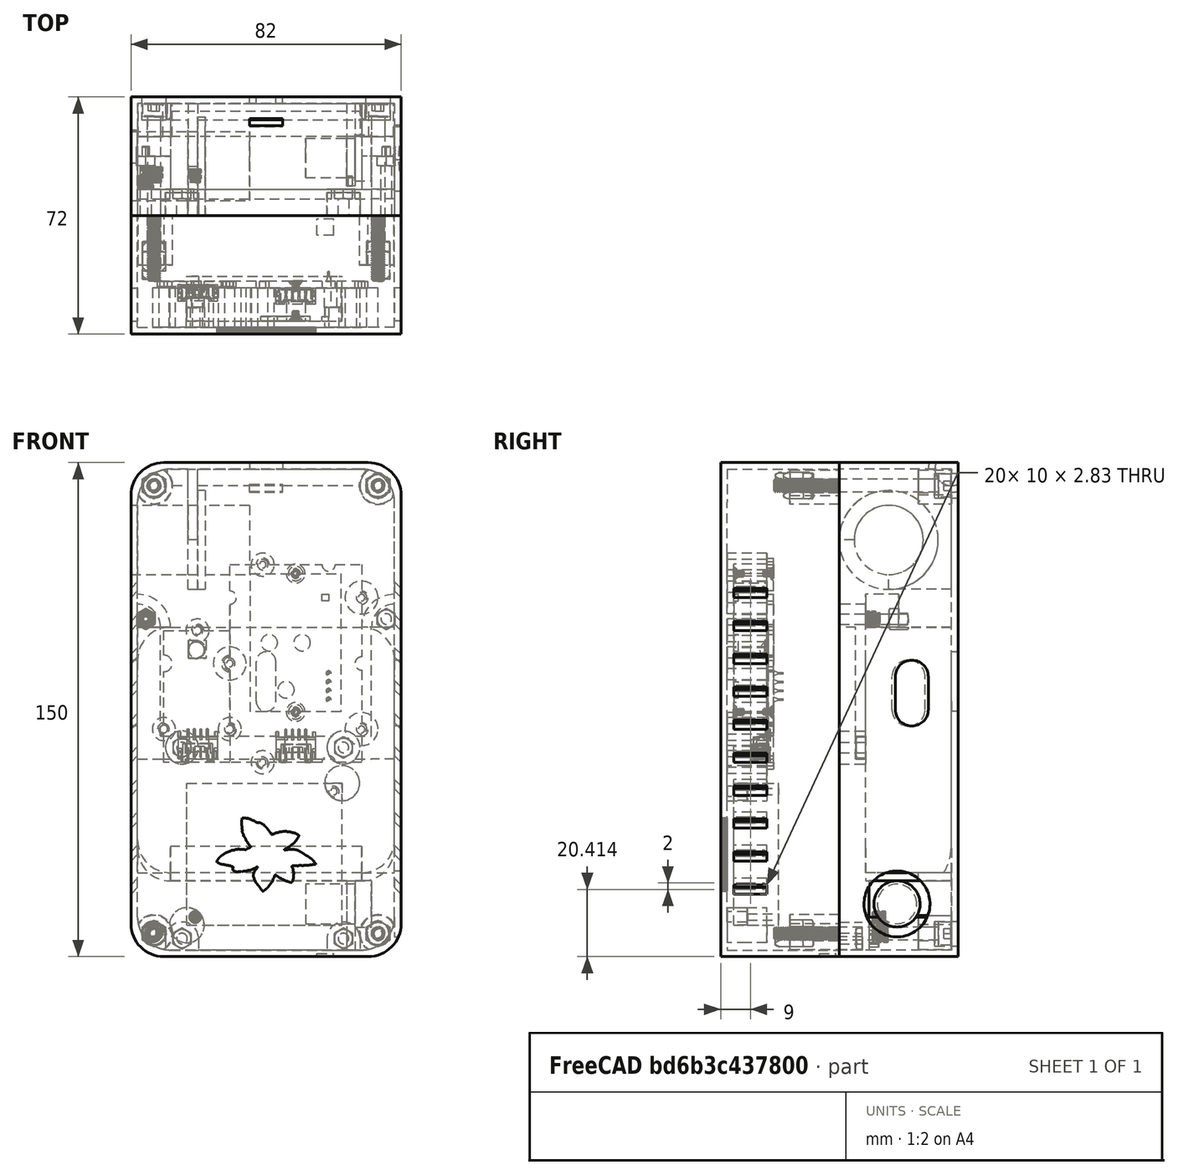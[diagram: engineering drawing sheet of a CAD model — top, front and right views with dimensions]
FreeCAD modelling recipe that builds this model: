
FCSTD DOCUMENT  (FreeCAD 0.20R29410 (Git))
Label: wearableRenewed_10_13_2022
License: All rights reserved
LicenseURL: http://en.wikipedia.org/wiki/All_rights_reserved
objects: Part::Cylinder×120, Part::MultiFuse×80, Part::Cut×73, Part::Box×72, Part::Feature×57, Part::FeaturePython×2
note: 404 computed .brp shape members not serialized (recipe doc carries the construction recipe); baked Part::Feature solids carry a one-line shape summary decoded from their .brp

FEATURE [Part::Feature] Feature  label="Odroid-C4"
  Placement = pos=(66,-10,0) rot=(0.57735,-0.57735,0.57735;2.0944rad)
  shape: bbox 57.1 x 20.65 x 89.5 mm, 2775 faces, 0 solids (baked)
FEATURE [Part::Feature] Feature001  label="SCD30"
  Placement = pos=(-1.3e-14,-22,57) rot=(0,-1,0;1.5708rad)
  shape: bbox 44 x 15.1 x 64 mm, 422 faces, 13 solids (baked)
FEATURE [Part::Feature] Feature002  label="bme280"
  Placement = pos=(-60,-20,58) rot=(0.707107,0,0.707107;3.14159rad)
  shape: bbox 23.8 x 6.016 x 41.9 mm, 221 faces, 2 solids (baked)
FEATURE [Part::MultiFuse] Fusion  label="i2cSensors"
  Placement = pos=(68,-10,0) rot=(0,0,1;0rad)
  Shapes = -> [Feature001,Feature002]
FEATURE [Part::Box] Box  label="ips7100"
  AttacherType = Attacher::AttachEngine3D
  Height = 43.1
  Length = 47.1
  Width = 13.55
FEATURE [Part::Cylinder] Cylinder
  Angle = 360
  AttacherType = Attacher::AttachEngine3D
  FirstAngle = 0
  Height = 13.55
  Placement = pos=(2.5,13.55,2.5) rot=(1,0,0;1.5708rad)
  Radius = 1
  SecondAngle = 0
FEATURE [Part::Cylinder] Cylinder001  label="semiCut"
  Angle = 90
  AttacherType = Attacher::AttachEngine3D
  FirstAngle = 0
  Height = 4.13
  Placement = pos=(0,4.13,-9e-16) rot=(1,0,0;1.5708rad)
  Radius = 5.25
  SecondAngle = 0
FEATURE [Part::MultiFuse] Fusion001  label="ipsCut"
  Shapes = -> [Cylinder,Cylinder001]
FEATURE [Part::Cylinder] Cylinder002
  Angle = 360
  AttacherType = Attacher::AttachEngine3D
  FirstAngle = 0
  Height = 13.55
  Placement = pos=(2.5,13.55,2.5) rot=(1,0,0;1.5708rad)
  Radius = 1
  SecondAngle = 0
FEATURE [Part::Cylinder] Cylinder003  label="semiCut001"
  Angle = 90
  AttacherType = Attacher::AttachEngine3D
  FirstAngle = 0
  Height = 4.13
  Placement = pos=(0,4.13,-9e-16) rot=(1,0,0;1.5708rad)
  Radius = 5.25
  SecondAngle = 0
FEATURE [Part::MultiFuse] Fusion002  label="ipsCut001"
  Placement = pos=(47.1,0,43.1) rot=(0,1,0;3.14159rad)
  Shapes = -> [Cylinder002,Cylinder003]
FEATURE [Part::MultiFuse] Fusion003
  Shapes = -> [Fusion001,Fusion002]
FEATURE [Part::Cut] Cut  label="ips7100V"
  Base = -> Box
  Placement = pos=(15,-42,7.55) rot=(0,0,1;0rad)
  Tool = -> Fusion003
FEATURE [Part::Box] Box001  label="V25B"
  AttacherType = Attacher::AttachEngine3D
  Height = 77
  Length = 78
  Width = 26
FEATURE [Part::Cylinder] Cylinder004
  Angle = 90
  AttacherType = Attacher::AttachEngine3D
  FirstAngle = 0
  Height = 26
  Placement = pos=(0,26,-5.8e-15) rot=(1,0,0;1.5708rad)
  Radius = 10
  SecondAngle = 0
FEATURE [Part::Box] Box002  label="Cube"
  AttacherType = Attacher::AttachEngine3D
  Height = 10
  Length = 10
  Width = 26
FEATURE [Part::Cut] Cut001
  Base = -> Box002
  Placement = pos=(68,0,67) rot=(0,0,1;0rad)
  Tool = -> Cylinder004
FEATURE [Part::Box] Box003  label="Cube001"
  AttacherType = Attacher::AttachEngine3D
  Height = 10
  Length = 10
  Width = 26
FEATURE [Part::Cylinder] Cylinder005
  Angle = 90
  AttacherType = Attacher::AttachEngine3D
  FirstAngle = 0
  Height = 26
  Placement = pos=(0,26,-5.8e-15) rot=(1,0,0;1.5708rad)
  Radius = 10
  SecondAngle = 0
FEATURE [Part::Cut] Cut002
  Base = -> Box003
  Placement = pos=(68,0,10) rot=(0,1,0;1.5708rad)
  Tool = -> Cylinder005
FEATURE [Part::Box] Box004  label="Cube002"
  AttacherType = Attacher::AttachEngine3D
  Height = 10
  Length = 10
  Width = 26
FEATURE [Part::Cylinder] Cylinder006
  Angle = 90
  AttacherType = Attacher::AttachEngine3D
  FirstAngle = 0
  Height = 26
  Placement = pos=(0,26,-5.8e-15) rot=(1,0,0;1.5708rad)
  Radius = 10
  SecondAngle = 0
FEATURE [Part::Cut] Cut003
  Base = -> Box004
  Placement = pos=(10,0,10) rot=(0,1,0;3.14159rad)
  Tool = -> Cylinder006
FEATURE [Part::Box] Box005  label="Cube003"
  AttacherType = Attacher::AttachEngine3D
  Height = 10
  Length = 10
  Width = 26
FEATURE [Part::Cylinder] Cylinder007
  Angle = 90
  AttacherType = Attacher::AttachEngine3D
  FirstAngle = 0
  Height = 26
  Placement = pos=(0,26,-5.8e-15) rot=(1,0,0;1.5708rad)
  Radius = 10
  SecondAngle = 0
FEATURE [Part::Cut] Cut004
  Base = -> Box005
  Placement = pos=(10,0,67) rot=(0,-1,0;1.5708rad)
  Tool = -> Cylinder007
FEATURE [Part::MultiFuse] Fusion004  label="v25Cuts"
  Shapes = -> [Cut001,Cut002,Cut003,Cut004]
FEATURE [Part::Cut] Cut005  label="V25B001"
  Base = -> Box001
  Placement = pos=(0,-2,21) rot=(0,0,1;0rad)
  Tool = -> Fusion004
FEATURE [Part::Box] Box007  label="Cube004"
  AttacherType = Attacher::AttachEngine3D
  Height = 10
  Length = 10
  Placement = pos=(0,-10,0) rot=(0,0,1;0rad)
  Width = 36
FEATURE [Part::Cylinder] Cylinder008
  Angle = 90
  AttacherType = Attacher::AttachEngine3D
  FirstAngle = 0
  Height = 36
  Placement = pos=(0,26,-5.8e-15) rot=(1,0,0;1.5708rad)
  Radius = 10
  SecondAngle = 0
FEATURE [Part::Cut] Cut006
  Base = -> Box007
  Placement = pos=(8,18,8) rot=(0.707107,0,-0.707107;3.14159rad)
  Tool = -> Cylinder008
FEATURE [Part::Box] Box008  label="baseOut001"
  AttacherType = Attacher::AttachEngine3D
  Height = 150
  Length = 82
  Placement = pos=(80,26,-2) rot=(0,0,1;3.14159rad)
  Width = 36
FEATURE [Part::Box] Box009  label="Cube005"
  AttacherType = Attacher::AttachEngine3D
  Height = 10
  Length = 10
  Placement = pos=(0,-10,0) rot=(0,0,1;0rad)
  Width = 36
FEATURE [Part::Cylinder] Cylinder009
  Angle = 90
  AttacherType = Attacher::AttachEngine3D
  FirstAngle = 0
  Height = 36
  Placement = pos=(0,26,-5.8e-15) rot=(1,0,0;1.5708rad)
  Radius = 10
  SecondAngle = 0
FEATURE [Part::Cut] Cut007
  Base = -> Box009
  Placement = pos=(70,18,8) rot=(1,0,0;3.14159rad)
  Tool = -> Cylinder009
FEATURE [Part::Box] Box010  label="Cube006"
  AttacherType = Attacher::AttachEngine3D
  Height = 10
  Length = 10
  Placement = pos=(0,-10,0) rot=(0,0,1;0rad)
  Width = 36
FEATURE [Part::Cylinder] Cylinder010
  Angle = 90
  AttacherType = Attacher::AttachEngine3D
  FirstAngle = 0
  Height = 36
  Placement = pos=(0,26,-5.8e-15) rot=(1,0,0;1.5708rad)
  Radius = 10
  SecondAngle = 0
FEATURE [Part::Cut] Cut008
  Base = -> Box010
  Placement = pos=(8,18,138) rot=(0,0,1;3.14159rad)
  Tool = -> Cylinder010
FEATURE [Part::Box] Box011  label="Cube007"
  AttacherType = Attacher::AttachEngine3D
  Height = 10
  Length = 10
  Placement = pos=(0,-10,0) rot=(0,0,1;0rad)
  Width = 36
FEATURE [Part::Cylinder] Cylinder011
  Angle = 90
  AttacherType = Attacher::AttachEngine3D
  FirstAngle = 0
  Height = 36
  Placement = pos=(0,26,-5.8e-15) rot=(1,0,0;1.5708rad)
  Radius = 10
  SecondAngle = 0
FEATURE [Part::Cut] Cut009
  Base = -> Box011
  Placement = pos=(70,18,138) rot=(0.707107,0,0.707107;3.14159rad)
  Tool = -> Cylinder011
FEATURE [Part::MultiFuse] Fusion005
  Placement = pos=(0,-2,0) rot=(0,0,1;0rad)
  Shapes = -> [Cut006,Cut007,Cut008,Cut009]
FEATURE [Part::Cut] Cut010  label="BaseOut"
  Base = -> Box008
  Tool = -> Fusion005
FEATURE [Part::Box] Box013  label="Cube009"
  AttacherType = Attacher::AttachEngine3D
  Height = 10
  Length = 10
  Placement = pos=(0,-8,0) rot=(0,0,1;0rad)
  Width = 34
FEATURE [Part::Box] Box014  label="baseOut002"
  AttacherType = Attacher::AttachEngine3D
  Height = 146
  Length = 78
  Placement = pos=(80,26,-2) rot=(0,0,1;3.14159rad)
  Width = 34
FEATURE [Part::Box] Box015  label="Cube010"
  AttacherType = Attacher::AttachEngine3D
  Height = 10
  Length = 10
  Placement = pos=(0,-8,0) rot=(0,0,1;0rad)
  Width = 34
FEATURE [Part::Box] Box016  label="Cube011"
  AttacherType = Attacher::AttachEngine3D
  Height = 10
  Length = 10
  Placement = pos=(0,-8,0) rot=(0,0,1;0rad)
  Width = 34
FEATURE [Part::Box] Box017  label="Cube012"
  AttacherType = Attacher::AttachEngine3D
  Height = 10
  Length = 10
  Placement = pos=(0,-8,0) rot=(0,0,1;0rad)
  Width = 34
FEATURE [Part::Cylinder] Cylinder013
  Angle = 90
  AttacherType = Attacher::AttachEngine3D
  FirstAngle = 0
  Height = 34
  Placement = pos=(0,26,-5.8e-15) rot=(1,0,0;1.5708rad)
  Radius = 10
  SecondAngle = 0
FEATURE [Part::Cut] Cut012
  Base = -> Box013
  Placement = pos=(12,18,8) rot=(0.707107,0,-0.707107;3.14159rad)
  Tool = -> Cylinder013
FEATURE [Part::Cylinder] Cylinder014
  Angle = 90
  AttacherType = Attacher::AttachEngine3D
  FirstAngle = 0
  Height = 34
  Placement = pos=(0,26,-5.8e-15) rot=(1,0,0;1.5708rad)
  Radius = 10
  SecondAngle = 0
FEATURE [Part::Cut] Cut013
  Base = -> Box015
  Placement = pos=(70,18,8) rot=(1,0,0;3.14159rad)
  Tool = -> Cylinder014
FEATURE [Part::Cylinder] Cylinder015
  Angle = 90
  AttacherType = Attacher::AttachEngine3D
  FirstAngle = 0
  Height = 34
  Placement = pos=(0,26,-5.8e-15) rot=(1,0,0;1.5708rad)
  Radius = 10
  SecondAngle = 0
FEATURE [Part::Cut] Cut014
  Base = -> Box016
  Placement = pos=(12,18,134) rot=(0,0,1;3.14159rad)
  Tool = -> Cylinder015
FEATURE [Part::Cylinder] Cylinder016
  Angle = 90
  AttacherType = Attacher::AttachEngine3D
  FirstAngle = 0
  Height = 34
  Placement = pos=(0,26,-5.8e-15) rot=(1,0,0;1.5708rad)
  Radius = 10
  SecondAngle = 0
FEATURE [Part::Cut] Cut015
  Base = -> Box017
  Placement = pos=(70,18,134) rot=(0.707107,0,0.707107;3.14159rad)
  Tool = -> Cylinder016
FEATURE [Part::MultiFuse] Fusion006
  Shapes = -> [Cut012,Cut013,Cut014,Cut015]
FEATURE [Part::Cut] Cut016  label="BaseOut001"
  Base = -> Box014
  Placement = pos=(-2,-2,2) rot=(0,0,1;0rad)
  Tool = -> Fusion006
FEATURE [Part::Cut] Cut017  label="baseOut"
  Base = -> Cut010
  Tool = -> Cut016
FEATURE [Part::Box] Box018  label="Cube013"
  AttacherType = Attacher::AttachEngine3D
  Height = 10
  Length = 10
  Placement = pos=(10,26,0) rot=(0,0,1;3.14159rad)
  Width = 26
FEATURE [Part::Cylinder] Cylinder017
  Angle = 90
  AttacherType = Attacher::AttachEngine3D
  FirstAngle = 0
  Height = 26
  Placement = pos=(0,26,-5.8e-15) rot=(1,0,0;1.5708rad)
  Radius = 10
  SecondAngle = 0
FEATURE [Part::Cut] Cut018  label="batterySupport"
  Base = -> Box018
  Placement = pos=(10,-2,33.5) rot=(0,1,0;3.14159rad)
  Tool = -> Cylinder017
FEATURE [Part::Box] Box019  label="Cube014"
  AttacherType = Attacher::AttachEngine3D
  Height = 10
  Length = 10
  Placement = pos=(10,26,0) rot=(0,0,1;3.14159rad)
  Width = 26
FEATURE [Part::Cylinder] Cylinder018
  Angle = 90
  AttacherType = Attacher::AttachEngine3D
  FirstAngle = 0
  Height = 26
  Placement = pos=(0,26,-5.8e-15) rot=(1,0,0;1.5708rad)
  Radius = 10
  SecondAngle = 0
FEATURE [Part::Cut] Cut019  label="batterySupport001"
  Base = -> Box019
  Placement = pos=(68,-2,33.5) rot=(0,1,0;1.5708rad)
  Tool = -> Cylinder018
FEATURE [Part::Box] Box020  label="Cube015"
  AttacherType = Attacher::AttachEngine3D
  Height = 10
  Length = 10
  Placement = pos=(10,26,0) rot=(0,0,1;3.14159rad)
  Width = 26
FEATURE [Part::Cylinder] Cylinder019
  Angle = 90
  AttacherType = Attacher::AttachEngine3D
  FirstAngle = 0
  Height = 26
  Placement = pos=(0,26,-5.8e-15) rot=(1,0,0;1.5708rad)
  Radius = 10
  SecondAngle = 0
FEATURE [Part::Cut] Cut020  label="batterySupport002"
  Base = -> Box020
  Placement = pos=(68,-2,88) rot=(0,0,1;0rad)
  Tool = -> Cylinder019
FEATURE [Part::Box] Box021  label="Cube016"
  AttacherType = Attacher::AttachEngine3D
  Height = 10
  Length = 10
  Placement = pos=(10,26,0) rot=(0,0,1;3.14159rad)
  Width = 26
FEATURE [Part::Cylinder] Cylinder020
  Angle = 90
  AttacherType = Attacher::AttachEngine3D
  FirstAngle = 0
  Height = 26
  Placement = pos=(0,26,-5.8e-15) rot=(1,0,0;1.5708rad)
  Radius = 10
  SecondAngle = 0
FEATURE [Part::Cut] Cut021  label="batterySupport003"
  Base = -> Box021
  Placement = pos=(10,-2,88) rot=(0,-1,0;1.5708rad)
  Tool = -> Cylinder020
FEATURE [Part::Cylinder] Cylinder021
  Angle = 360
  AttacherType = Attacher::AttachEngine3D
  FirstAngle = 0
  Height = 7
  Placement = pos=(13.5,-3,3.5) rot=(1,0,0;1.5708rad)
  Radius = 5
  SecondAngle = 0
FEATURE [Part::Cylinder] Cylinder022
  Angle = 360
  AttacherType = Attacher::AttachEngine3D
  FirstAngle = 0
  Height = 8
  Placement = pos=(13.5,-2,3.5) rot=(1,0,0;1.5708rad)
  Radius = 1.6
  SecondAngle = 0
FEATURE [Part::Box] Box022  label="Cube017"
  AttacherType = Attacher::AttachEngine3D
  Height = 4
  Length = 10
  Placement = pos=(8.5,-3,4) rot=(1,0,0;3.14159rad)
  Width = 7
FEATURE [Part::Cylinder] Cylinder023
  Angle = 360
  AttacherType = Attacher::AttachEngine3D
  FirstAngle = 0
  Height = 7
  Placement = pos=(62.5,-3,3.5) rot=(1,0,0;1.5708rad)
  Radius = 5
  SecondAngle = 0
FEATURE [Part::Cylinder] Cylinder024
  Angle = 360
  AttacherType = Attacher::AttachEngine3D
  FirstAngle = 0
  Height = 8
  Placement = pos=(62.5,-2,3.5) rot=(1,0,0;1.5708rad)
  Radius = 1.6
  SecondAngle = 0
FEATURE [Part::Box] Box023  label="Cube018"
  AttacherType = Attacher::AttachEngine3D
  Height = 4
  Length = 10
  Placement = pos=(57.5,-3,4) rot=(1,0,0;3.14159rad)
  Width = 7
FEATURE [Part::Cylinder] Cylinder025
  Angle = 360
  AttacherType = Attacher::AttachEngine3D
  FirstAngle = 0
  Height = 20
  Radius = 6
  SecondAngle = 0
FEATURE [Part::Cylinder] Cylinder026
  Angle = 360
  AttacherType = Attacher::AttachEngine3D
  FirstAngle = 0
  Height = 5
  Radius = 7
  SecondAngle = 0
FEATURE [Part::MultiFuse] Fusion007  label="powerSwitch"
  Placement = pos=(71,7.5,14) rot=(0,-1,0;1.5708rad)
  Shapes = -> [Cylinder025,Cylinder026]
FEATURE [Part::Box] Box024  label="Cube019"
  AttacherType = Attacher::AttachEngine3D
  Height = 22
  Length = 2.5
  Placement = pos=(63.5,24,21) rot=(1,0,0;3.14159rad)
  Width = 25
FEATURE [Part::MultiFuse] Fusion008  label="base"
  Shapes = -> [Cut017,Cut018,Cut019,Cut020,Cut021]
FEATURE [Part::MultiFuse] Fusion009  label="base001"
  Shapes = -> [Cylinder021,Cylinder023,Box022,Box023,Box024,Fusion008]
FEATURE [Part::MultiFuse] Fusion010  label="baseCuts"
  Shapes = -> [Cylinder024,Cylinder022,Fusion007]
FEATURE [Part::Cut] Cut022  label="base002"
  Base = -> Fusion009
  Tool = -> Fusion010
FEATURE [Part::Cylinder] Cylinder027  label="mainMounts"
  Angle = 90
  AttacherType = Attacher::AttachEngine3D
  FirstAngle = 0
  Height = 10
  Placement = pos=(0,24,98) rot=(1,0,0;1.5708rad)
  Radius = 10
  SecondAngle = 0
FEATURE [Part::Cylinder] Cylinder028  label="mainMounts001"
  Angle = 90
  AttacherType = Attacher::AttachEngine3D
  FirstAngle = 0
  Height = 10
  Placement = pos=(78,24,98) rot=(0.57735,-0.57735,0.57735;2.0944rad)
  Radius = 10
  SecondAngle = 0
FEATURE [Part::Cylinder] Cylinder029
  Angle = 360
  AttacherType = Attacher::AttachEngine3D
  FirstAngle = 0
  Height = 10
  Placement = pos=(2.5,-2,100.5) rot=(1,0,0;1.5708rad)
  Radius = 1.6
  SecondAngle = 0
FEATURE [Part::Cylinder] Cylinder030
  Angle = 360
  AttacherType = Attacher::AttachEngine3D
  FirstAngle = 0
  Height = 10
  Placement = pos=(75.5,-2,100.5) rot=(1,0,0;1.5708rad)
  Radius = 1.6
  SecondAngle = 0
FEATURE [Part::MultiFuse] Fusion011  label="baseCuts001"
  Placement = pos=(0,10,0) rot=(0,0,1;0rad)
  Shapes = -> [Cylinder029,Cylinder030]
FEATURE [Part::MultiFuse] Fusion012
  Placement = pos=(0,-16,0) rot=(0,0,1;0rad)
  Shapes = -> [Cylinder028,Cylinder027]
FEATURE [Part::MultiFuse] Fusion013  label="base003"
  Shapes = -> [Cut022,Fusion012]
FEATURE [Part::Cut] Cut023  label="baseBottom"
  Base = -> Fusion013
  Tool = -> Fusion011
FEATURE [Part::Feature] Solid  label="m3HeatSet"
  Placement = pos=(2.5,2.3,100.5) rot=(1,0,0;3.14159rad)
  shape: bbox 4.772 x 4.354 x 4.772 mm, 239 faces (baked)
FEATURE [Part::Cylinder] Cylinder031
  Angle = 360
  AttacherType = Attacher::AttachEngine3D
  FirstAngle = 0
  Height = 8
  Placement = pos=(13.5,-2,61.5) rot=(1,0,0;1.5708rad)
  Radius = 5
  SecondAngle = 0
FEATURE [Part::Cylinder] Cylinder032  label="cuts"
  Angle = 360
  AttacherType = Attacher::AttachEngine3D
  FirstAngle = 0
  Height = 8
  Placement = pos=(13.5,-2,61.5) rot=(1,0,0;1.5708rad)
  Radius = 1.6
  SecondAngle = 0
FEATURE [Part::Cylinder] Cylinder034
  Angle = 360
  AttacherType = Attacher::AttachEngine3D
  FirstAngle = 0
  Height = 8
  Placement = pos=(62.5,-2,61.5) rot=(1,0,0;1.5708rad)
  Radius = 5
  SecondAngle = 0
FEATURE [Part::Cylinder] Cylinder035  label="cuts001"
  Angle = 360
  AttacherType = Attacher::AttachEngine3D
  FirstAngle = 0
  Height = 8
  Placement = pos=(62.5,-2,61.5) rot=(1,0,0;1.5708rad)
  Radius = 1.6
  SecondAngle = 0
FEATURE [Part::Cylinder] Cylinder036
  Angle = 90
  AttacherType = Attacher::AttachEngine3D
  FirstAngle = 0
  Height = 8
  Placement = pos=(78,-2,98) rot=(0.57735,-0.57735,0.57735;2.0944rad)
  Radius = 7
  SecondAngle = 0
FEATURE [Part::Cylinder] Cylinder037
  Angle = 90
  AttacherType = Attacher::AttachEngine3D
  FirstAngle = 0
  Height = 8
  Placement = pos=(0,-2,98) rot=(1,0,0;1.5708rad)
  Radius = 7
  SecondAngle = 0
FEATURE [Part::Box] Box025  label="Cube020"
  AttacherType = Attacher::AttachEngine3D
  Height = 7
  Length = 78
  Placement = pos=(0,-5,58) rot=(0,0,1;0rad)
  Width = 3
FEATURE [Part::Box] Box026  label="Cube021"
  AttacherType = Attacher::AttachEngine3D
  Height = 7
  Length = 40
  Placement = pos=(7,-5,58) rot=(0,-1,0;1.5708rad)
  Width = 3
FEATURE [Part::Box] Box027  label="Cube022"
  AttacherType = Attacher::AttachEngine3D
  Height = 7
  Length = 40
  Placement = pos=(78,-5,58) rot=(0,-1,0;1.5708rad)
  Width = 3
FEATURE [Part::MultiFuse] Fusion014
  Shapes = -> [Box027,Box025,Box026,Cylinder034,Cylinder031]
FEATURE [Part::Cylinder] Cylinder038  label="m3Screw"
  Angle = 360
  AttacherType = Attacher::AttachEngine3D
  FirstAngle = 0
  Height = 8
  Placement = pos=(75.5,-2,100.5) rot=(1,0,0;1.5708rad)
  Radius = 1.6
  SecondAngle = 0
FEATURE [Part::Cylinder] Cylinder039  label="m3Screw001"
  Angle = 360
  AttacherType = Attacher::AttachEngine3D
  FirstAngle = 0
  Height = 8
  Placement = pos=(2.5,-2,100.5) rot=(1,0,0;1.5708rad)
  Radius = 1.6
  SecondAngle = 0
FEATURE [Part::MultiFuse] Fusion015  label="c4Hold"
  Shapes = -> [Cylinder036,Cylinder037,Fusion014]
FEATURE [Part::MultiFuse] Fusion016  label="c4oldCuts"
  Shapes = -> [Cylinder039,Cylinder032,Cylinder035,Cylinder038]
FEATURE [Part::Cut] Cut024  label="c4Hold001"
  Base = -> Fusion015
  Tool = -> Fusion016
FEATURE [Part::Box] Box028  label="Cube023"
  AttacherType = Attacher::AttachEngine3D
  Height = 10
  Length = 10
  Placement = pos=(0,-10,0) rot=(0,0,1;0rad)
  Width = 36
FEATURE [Part::Box] Box029  label="baseOut003"
  AttacherType = Attacher::AttachEngine3D
  Height = 150
  Length = 82
  Placement = pos=(80,26,-2) rot=(0,0,1;3.14159rad)
  Width = 36
FEATURE [Part::Box] Box030  label="Cube024"
  AttacherType = Attacher::AttachEngine3D
  Height = 10
  Length = 10
  Placement = pos=(0,-10,0) rot=(0,0,1;0rad)
  Width = 36
FEATURE [Part::Box] Box031  label="Cube025"
  AttacherType = Attacher::AttachEngine3D
  Height = 10
  Length = 10
  Placement = pos=(0,-10,0) rot=(0,0,1;0rad)
  Width = 36
FEATURE [Part::Box] Box032  label="Cube026"
  AttacherType = Attacher::AttachEngine3D
  Height = 10
  Length = 10
  Placement = pos=(0,-10,0) rot=(0,0,1;0rad)
  Width = 36
FEATURE [Part::Box] Box033  label="Cube027"
  AttacherType = Attacher::AttachEngine3D
  Height = 10
  Length = 10
  Placement = pos=(0,-8,0) rot=(0,0,1;0rad)
  Width = 34
FEATURE [Part::Box] Box034  label="baseOut004"
  AttacherType = Attacher::AttachEngine3D
  Height = 146
  Length = 78
  Placement = pos=(80,26,-2) rot=(0,0,1;3.14159rad)
  Width = 34
FEATURE [Part::Box] Box035  label="Cube028"
  AttacherType = Attacher::AttachEngine3D
  Height = 10
  Length = 10
  Placement = pos=(0,-8,0) rot=(0,0,1;0rad)
  Width = 34
FEATURE [Part::Box] Box036  label="Cube029"
  AttacherType = Attacher::AttachEngine3D
  Height = 10
  Length = 10
  Placement = pos=(0,-8,0) rot=(0,0,1;0rad)
  Width = 34
FEATURE [Part::Box] Box037  label="Cube030"
  AttacherType = Attacher::AttachEngine3D
  Height = 10
  Length = 10
  Placement = pos=(0,-8,0) rot=(0,0,1;0rad)
  Width = 34
FEATURE [Part::Cylinder] Cylinder040
  Angle = 90
  AttacherType = Attacher::AttachEngine3D
  FirstAngle = 0
  Height = 36
  Placement = pos=(0,26,-5.8e-15) rot=(1,0,0;1.5708rad)
  Radius = 10
  SecondAngle = 0
FEATURE [Part::Cut] Cut025
  Base = -> Box028
  Placement = pos=(8,18,8) rot=(0.707107,0,-0.707107;3.14159rad)
  Tool = -> Cylinder040
FEATURE [Part::Cylinder] Cylinder041
  Angle = 90
  AttacherType = Attacher::AttachEngine3D
  FirstAngle = 0
  Height = 36
  Placement = pos=(0,26,-5.8e-15) rot=(1,0,0;1.5708rad)
  Radius = 10
  SecondAngle = 0
FEATURE [Part::Cut] Cut026
  Base = -> Box030
  Placement = pos=(70,18,8) rot=(1,0,0;3.14159rad)
  Tool = -> Cylinder041
FEATURE [Part::Cylinder] Cylinder042
  Angle = 90
  AttacherType = Attacher::AttachEngine3D
  FirstAngle = 0
  Height = 36
  Placement = pos=(0,26,-5.8e-15) rot=(1,0,0;1.5708rad)
  Radius = 10
  SecondAngle = 0
FEATURE [Part::Cut] Cut027
  Base = -> Box031
  Placement = pos=(8,18,138) rot=(0,0,1;3.14159rad)
  Tool = -> Cylinder042
FEATURE [Part::Cylinder] Cylinder043
  Angle = 90
  AttacherType = Attacher::AttachEngine3D
  FirstAngle = 0
  Height = 36
  Placement = pos=(0,26,-5.8e-15) rot=(1,0,0;1.5708rad)
  Radius = 10
  SecondAngle = 0
FEATURE [Part::Cut] Cut028
  Base = -> Box032
  Placement = pos=(70,18,138) rot=(0.707107,0,0.707107;3.14159rad)
  Tool = -> Cylinder043
FEATURE [Part::Cylinder] Cylinder044
  Angle = 90
  AttacherType = Attacher::AttachEngine3D
  FirstAngle = 0
  Height = 34
  Placement = pos=(0,26,-5.8e-15) rot=(1,0,0;1.5708rad)
  Radius = 10
  SecondAngle = 0
FEATURE [Part::Cut] Cut030
  Base = -> Box033
  Placement = pos=(12,18,8) rot=(0.707107,0,-0.707107;3.14159rad)
  Tool = -> Cylinder044
FEATURE [Part::Cylinder] Cylinder045
  Angle = 90
  AttacherType = Attacher::AttachEngine3D
  FirstAngle = 0
  Height = 34
  Placement = pos=(0,26,-5.8e-15) rot=(1,0,0;1.5708rad)
  Radius = 10
  SecondAngle = 0
FEATURE [Part::Cut] Cut031
  Base = -> Box035
  Placement = pos=(70,18,8) rot=(1,0,0;3.14159rad)
  Tool = -> Cylinder045
FEATURE [Part::Cylinder] Cylinder046
  Angle = 90
  AttacherType = Attacher::AttachEngine3D
  FirstAngle = 0
  Height = 34
  Placement = pos=(0,26,-5.8e-15) rot=(1,0,0;1.5708rad)
  Radius = 10
  SecondAngle = 0
FEATURE [Part::Cut] Cut032
  Base = -> Box036
  Placement = pos=(12,18,134) rot=(0,0,1;3.14159rad)
  Tool = -> Cylinder046
FEATURE [Part::Cylinder] Cylinder047
  Angle = 90
  AttacherType = Attacher::AttachEngine3D
  FirstAngle = 0
  Height = 34
  Placement = pos=(0,26,-5.8e-15) rot=(1,0,0;1.5708rad)
  Radius = 10
  SecondAngle = 0
FEATURE [Part::Cut] Cut033
  Base = -> Box037
  Placement = pos=(70,18,134) rot=(0.707107,0,0.707107;3.14159rad)
  Tool = -> Cylinder047
FEATURE [Part::MultiFuse] Fusion017
  Placement = pos=(0,-2,0) rot=(0,0,1;0rad)
  Shapes = -> [Cut025,Cut026,Cut027,Cut028]
FEATURE [Part::Cut] Cut029  label="BaseOut002"
  Base = -> Box029
  Tool = -> Fusion017
FEATURE [Part::MultiFuse] Fusion018
  Shapes = -> [Cut030,Cut031,Cut032,Cut033]
FEATURE [Part::Cut] Cut034  label="BaseOut003"
  Base = -> Box034
  Placement = pos=(-2,-2,2) rot=(0,0,1;0rad)
  Tool = -> Fusion018
FEATURE [Part::Cut] Cut035  label="baseTop"
  Base = -> Cut029
  Placement = pos=(78,-20,0) rot=(0,0,1;3.14159rad)
  Tool = -> Cut034
FEATURE [Part::Feature] Solid001  label="m2HeatSet"
  Placement = pos=(17.5,0,10) rot=(0,0,1;0rad)
  shape: bbox 3.655 x 4.083 x 3.655 mm, 239 faces (baked)
FEATURE [Part::Cylinder] Cylinder048
  Angle = 360
  AttacherType = Attacher::AttachEngine3D
  FirstAngle = 0
  Height = 6
  Placement = pos=(17.5,-44,10.05) rot=(-1,0,0;1.5708rad)
  Radius = 1.57
  SecondAngle = 0
FEATURE [Part::Cylinder] Cylinder049
  Angle = 360
  AttacherType = Attacher::AttachEngine3D
  FirstAngle = 0
  Height = 6
  Placement = pos=(15,-44,7.55) rot=(0.57735,0.57735,0.57735;4.18879rad)
  Radius = 5.3
  SecondAngle = 0
FEATURE [Part::Cylinder] Cylinder050
  Angle = 360
  AttacherType = Attacher::AttachEngine3D
  FirstAngle = 0
  Height = 6
  Placement = pos=(62.1,-44,50.65) rot=(0.57735,-0.57735,-0.57735;4.18879rad)
  Radius = 5.3
  SecondAngle = 0
FEATURE [Part::Cylinder] Cylinder051
  Angle = 360
  AttacherType = Attacher::AttachEngine3D
  FirstAngle = 0
  Height = 6
  Placement = pos=(59.6,-44,48.15) rot=(-1,0,0;1.5708rad)
  Radius = 1.57
  SecondAngle = 0
FEATURE [Part::Cut] Cut036
  Base = -> Cylinder049
  Tool = -> Cylinder048
FEATURE [Part::Cut] Cut037
  Base = -> Cylinder050
  Tool = -> Cylinder051
FEATURE [Part::Cylinder] Cylinder052
  Angle = 270
  AttacherType = Attacher::AttachEngine3D
  FirstAngle = 0
  Height = 6
  Placement = pos=(15,-38,7.55) rot=(-1,0,0;1.5708rad)
  Radius = 5.3
  SecondAngle = 0
FEATURE [Part::Cylinder] Cylinder053
  Angle = 270
  AttacherType = Attacher::AttachEngine3D
  FirstAngle = 0
  Height = 6
  Placement = pos=(62.1,-38,50.65) rot=(0,0.707107,0.707107;3.14159rad)
  Radius = 5.3
  SecondAngle = 0
FEATURE [Part::MultiFuse] Fusion019  label="baseTop001"
  Shapes = -> [Cut036,Cut037,Cylinder052,Cylinder053,Cut035]
FEATURE [Part::Cylinder] Cylinder054  label="m2HeatSet001"
  Angle = 360
  AttacherType = Attacher::AttachEngine3D
  FirstAngle = 0
  Height = 12
  Placement = pos=(8,-44,67.1) rot=(-1,0,0;1.5708rad)
  Radius = 1.6
  SecondAngle = 0
FEATURE [Part::Cylinder] Cylinder055  label="m2HeatSet002"
  Angle = 360
  AttacherType = Attacher::AttachEngine3D
  FirstAngle = 0
  Height = 12
  Placement = pos=(28,-44,67.1) rot=(-1,0,0;1.5708rad)
  Radius = 1.6
  SecondAngle = 0
FEATURE [Part::Cylinder] Cylinder056  label="m2HeatSet003"
  Angle = 360
  AttacherType = Attacher::AttachEngine3D
  FirstAngle = 0
  Height = 12
  Placement = pos=(68,-44,67.1) rot=(-1,0,0;1.5708rad)
  Radius = 1.6
  SecondAngle = 0
FEATURE [Part::Cylinder] Cylinder057  label="m2HeatSet004"
  Angle = 360
  AttacherType = Attacher::AttachEngine3D
  FirstAngle = 0
  Height = 12
  Placement = pos=(18.2,-44,97) rot=(-1,0,0;1.5708rad)
  Radius = 1.6
  SecondAngle = 0
FEATURE [Part::Cylinder] Cylinder058  label="m2HeatSet005"
  Angle = 360
  AttacherType = Attacher::AttachEngine3D
  FirstAngle = 0
  Height = 12
  Placement = pos=(28,-44,87) rot=(-1,0,0;1.5708rad)
  Radius = 1.6
  SecondAngle = 0
FEATURE [Part::Cylinder] Cylinder059  label="m2HeatSet006"
  Angle = 360
  AttacherType = Attacher::AttachEngine3D
  FirstAngle = 0
  Height = 12
  Placement = pos=(38,-44,117) rot=(-1,0,0;1.5708rad)
  Radius = 1.6
  SecondAngle = 0
FEATURE [Part::Cylinder] Cylinder060  label="m2HeatSet007"
  Angle = 360
  AttacherType = Attacher::AttachEngine3D
  FirstAngle = 0
  Height = 12
  Placement = pos=(38,-44,57) rot=(-1,0,0;1.5708rad)
  Radius = 1.6
  SecondAngle = 0
FEATURE [Part::Cylinder] Cylinder061  label="m2HeatSet008"
  Angle = 360
  AttacherType = Attacher::AttachEngine3D
  FirstAngle = 0
  Height = 12
  Placement = pos=(68,-44,107) rot=(-1,0,0;1.5708rad)
  Radius = 1.6
  SecondAngle = 0
FEATURE [Part::Cylinder] Cylinder062  label="m2HeatSetOut"
  Angle = 360
  AttacherType = Attacher::AttachEngine3D
  FirstAngle = 0
  Height = 12
  Placement = pos=(8,-44,67.1) rot=(-1,0,0;1.5708rad)
  Radius = 3.5
  SecondAngle = 0
FEATURE [Part::Cylinder] Cylinder063  label="m2HeatSetOut001"
  Angle = 360
  AttacherType = Attacher::AttachEngine3D
  FirstAngle = 0
  Height = 12
  Placement = pos=(28,-44,67.1) rot=(-1,0,0;1.5708rad)
  Radius = 3.5
  SecondAngle = 0
FEATURE [Part::Cylinder] Cylinder064  label="m2HeatSetOut002"
  Angle = 360
  AttacherType = Attacher::AttachEngine3D
  FirstAngle = 0
  Height = 12
  Placement = pos=(18.2,-44,97) rot=(-1,0,0;1.5708rad)
  Radius = 3.5
  SecondAngle = 0
FEATURE [Part::Cylinder] Cylinder065  label="m2HeatSetOut003"
  Angle = 360
  AttacherType = Attacher::AttachEngine3D
  FirstAngle = 0
  Height = 12
  Placement = pos=(68,-44,67.1) rot=(-1,0,0;1.5708rad)
  Radius = 5
  SecondAngle = 0
FEATURE [Part::Cylinder] Cylinder066  label="m2HeatSetOut004"
  Angle = 360
  AttacherType = Attacher::AttachEngine3D
  FirstAngle = 0
  Height = 12
  Placement = pos=(28,-44,87) rot=(-1,0,0;1.5708rad)
  Radius = 5
  SecondAngle = 0
FEATURE [Part::Cylinder] Cylinder067  label="m2HeatSetOut005"
  Angle = 360
  AttacherType = Attacher::AttachEngine3D
  FirstAngle = 0
  Height = 12
  Placement = pos=(38,-44,57) rot=(-1,0,0;1.5708rad)
  Radius = 3.5
  SecondAngle = 0
FEATURE [Part::Cylinder] Cylinder068  label="m2HeatSetOut006"
  Angle = 360
  AttacherType = Attacher::AttachEngine3D
  FirstAngle = 0
  Height = 12
  Placement = pos=(68,-44,107) rot=(-1,0,0;1.5708rad)
  Radius = 5
  SecondAngle = 0
FEATURE [Part::Cylinder] Cylinder069  label="m2HeatSetOut007"
  Angle = 360
  AttacherType = Attacher::AttachEngine3D
  FirstAngle = 0
  Height = 12
  Placement = pos=(38,-44,117) rot=(-1,0,0;1.5708rad)
  Radius = 3.5
  SecondAngle = 0
FEATURE [Part::MultiFuse] Fusion020  label="baseTop002"
  Shapes = -> [Cylinder069,Cylinder063,Cylinder064,Cylinder065,Cylinder066,Cylinder067,Cylinder068,Fusion019]
FEATURE [Part::MultiFuse] Fusion021  label="m2HeatSetCuts"
  Shapes = -> [Cylinder062,Cylinder054,Cylinder055,Cylinder056,Cylinder057,Cylinder058,Cylinder059,Cylinder060,Cylinder061]
FEATURE [Part::Cut] Cut038  label="baseTop003"
  Base = -> Fusion020
  Tool = -> Fusion021
FEATURE [Part::Cylinder] Cylinder070
  Angle = 360
  AttacherType = Attacher::AttachEngine3D
  FirstAngle = 0
  Height = 20
  Radius = 6
  SecondAngle = 0
FEATURE [Part::Cylinder] Cylinder071
  Angle = 360
  AttacherType = Attacher::AttachEngine3D
  FirstAngle = 0
  Height = 5
  Radius = 7
  SecondAngle = 0
FEATURE [Part::MultiFuse] Fusion022  label="powerSwitch001"
  Placement = pos=(71,7.5,14) rot=(0,-1,0;1.5708rad)
  Shapes = -> [Cylinder070,Cylinder071]
FEATURE [Part::Feature] Solid002  label="M4Screw"
  Placement = pos=(73,-30,5) rot=(0.57735,-0.57735,0.57735;2.0944rad)
  shape: bbox 7.001 x 54.15 x 7.001 mm, 147 faces (baked)
FEATURE [Part::Feature] Solid003  label="M4Screw001"
  Placement = pos=(5,-30,5) rot=(0.57735,-0.57735,0.57735;2.0944rad)
  shape: bbox 7.001 x 54.15 x 7.001 mm, 147 faces (baked)
FEATURE [Part::Feature] Solid004  label="M4Screw002"
  Placement = pos=(5,-30,141) rot=(0.57735,-0.57735,0.57735;2.0944rad)
  shape: bbox 7.001 x 54.15 x 7.001 mm, 147 faces (baked)
FEATURE [Part::Feature] Solid005  label="M4Screw003"
  Placement = pos=(73,-30,141) rot=(0.57735,-0.57735,0.57735;2.0944rad)
  shape: bbox 7.001 x 54.15 x 7.001 mm, 147 faces (baked)
FEATURE [Part::Cylinder] Cylinder073  label="m4SupportDisk"
  Angle = 360
  AttacherType = Attacher::AttachEngine3D
  FirstAngle = 0
  Height = 15
  Placement = pos=(5,-25,141) rot=(-1,0,0;1.5708rad)
  Radius = 5.69
  SecondAngle = 0
FEATURE [Part::Feature] Solid006  label="m4HeatSet"
  Placement = pos=(4.5,0,5.5) rot=(0,0,1;0rad)
  shape: bbox 6.396 x 4.801 x 6.396 mm, 237 faces (baked)
FEATURE [Part::Cylinder] Cylinder080  label="m2HeatSetOut008"
  Angle = 360
  AttacherType = Attacher::AttachEngine3D
  FirstAngle = 0
  Height = 12
  Placement = pos=(8,-44,67.1) rot=(-1,0,0;1.5708rad)
  Radius = 3.5
  SecondAngle = 0
FEATURE [Part::Cylinder] Cylinder081  label="m2HeatSet009"
  Angle = 360
  AttacherType = Attacher::AttachEngine3D
  FirstAngle = 0
  Height = 12
  Placement = pos=(8,-44,67.1) rot=(-1,0,0;1.5708rad)
  Radius = 1.6
  SecondAngle = 0
FEATURE [Part::Cut] Cut043  label="m2HeatSet010"
  Base = -> Cylinder080
  Tool = -> Cylinder081
FEATURE [Part::Cylinder] Cylinder084  label="m4HoleBase006"
  Angle = 360
  AttacherType = Attacher::AttachEngine3D
  FirstAngle = 0
  Height = 12
  Placement = pos=(73,26,5) rot=(0,0.707107,-0.707107;3.14159rad)
  Radius = 5.5
  SecondAngle = 0
FEATURE [Part::Cylinder] Cylinder085  label="m4HoleBaseCut"
  Angle = 360
  AttacherType = Attacher::AttachEngine3D
  FirstAngle = 0
  Height = 7
  Placement = pos=(73,26,5) rot=(0,0.707107,-0.707107;3.14159rad)
  Radius = 3.75
  SecondAngle = 0
FEATURE [Part::Cylinder] Cylinder086  label="m4HoleBase007"
  Angle = 360
  AttacherType = Attacher::AttachEngine3D
  FirstAngle = 0
  Height = 12
  Placement = pos=(5,26,5) rot=(0,0.707107,-0.707107;3.14159rad)
  Radius = 5.5
  SecondAngle = 0
FEATURE [Part::Cylinder] Cylinder087  label="m4HoleBaseCut001"
  Angle = 360
  AttacherType = Attacher::AttachEngine3D
  FirstAngle = 0
  Height = 7
  Placement = pos=(5,26,5) rot=(0,0.707107,-0.707107;3.14159rad)
  Radius = 3.75
  SecondAngle = 0
FEATURE [Part::Cylinder] Cylinder088  label="m4HoleBase008"
  Angle = 360
  AttacherType = Attacher::AttachEngine3D
  FirstAngle = 0
  Height = 12
  Placement = pos=(73,26,141) rot=(0,0.707107,-0.707107;3.14159rad)
  Radius = 5.5
  SecondAngle = 0
FEATURE [Part::Cylinder] Cylinder089  label="m4HoleBaseCut002"
  Angle = 360
  AttacherType = Attacher::AttachEngine3D
  FirstAngle = 0
  Height = 7
  Placement = pos=(73,26,141) rot=(0,0.707107,-0.707107;3.14159rad)
  Radius = 3.75
  SecondAngle = 0
FEATURE [Part::Cylinder] Cylinder090  label="m4HoleBase009"
  Angle = 360
  AttacherType = Attacher::AttachEngine3D
  FirstAngle = 0
  Height = 12
  Placement = pos=(5,26,141) rot=(0,0.707107,-0.707107;3.14159rad)
  Radius = 5.5
  SecondAngle = 0
FEATURE [Part::Cylinder] Cylinder091  label="m4HoleBaseCut003"
  Angle = 360
  AttacherType = Attacher::AttachEngine3D
  FirstAngle = 0
  Height = 7
  Placement = pos=(5,26,141) rot=(0,0.707107,-0.707107;3.14159rad)
  Radius = 3.75
  SecondAngle = 0
FEATURE [Part::MultiFuse] Fusion025  label="baseBottom001"
  Shapes = -> [Cylinder084,Cylinder086,Cylinder088,Cylinder090,Cut023]
FEATURE [Part::MultiFuse] Fusion026  label="m4Cuts"
  Shapes = -> [Cylinder085,Cylinder087,Cylinder089,Cylinder091]
FEATURE [Part::Cut] Cut044  label="baseBottom002"
  Base = -> Fusion025
  Tool = -> Fusion026
FEATURE [Part::Cylinder] Cylinder092  label="m4HoleBaseCut004"
  Angle = 360
  AttacherType = Attacher::AttachEngine3D
  FirstAngle = 0
  Height = 7
  Placement = pos=(73,26,5) rot=(0,0.707107,-0.707107;3.14159rad)
  Radius = 2.1
  SecondAngle = 0
FEATURE [Part::Cylinder] Cylinder093  label="m4HoleBaseCut005"
  Angle = 360
  AttacherType = Attacher::AttachEngine3D
  FirstAngle = 0
  Height = 7
  Placement = pos=(5,26,5) rot=(0,0.707107,-0.707107;3.14159rad)
  Radius = 2.1
  SecondAngle = 0
FEATURE [Part::Cylinder] Cylinder094  label="m4HoleBaseCut006"
  Angle = 360
  AttacherType = Attacher::AttachEngine3D
  FirstAngle = 0
  Height = 7
  Placement = pos=(73,26,141) rot=(0,0.707107,-0.707107;3.14159rad)
  Radius = 2.1
  SecondAngle = 0
FEATURE [Part::Cylinder] Cylinder095  label="m4HoleBaseCut007"
  Angle = 360
  AttacherType = Attacher::AttachEngine3D
  FirstAngle = 0
  Height = 7
  Placement = pos=(5,26,141) rot=(0,0.707107,-0.707107;3.14159rad)
  Radius = 2.1
  SecondAngle = 0
FEATURE [Part::MultiFuse] Fusion027  label="m4Cuts001"
  Placement = pos=(0,-5,0) rot=(0,0,1;0rad)
  Shapes = -> [Cylinder092,Cylinder093,Cylinder094,Cylinder095]
FEATURE [Part::Cut] Cut045  label="baseBottom003"
  Base = -> Cut044
  Tool = -> Fusion027
FEATURE [Part::Cylinder] Cylinder096
  Angle = 360
  AttacherType = Attacher::AttachEngine3D
  FirstAngle = 0
  Height = 20
  Radius = 6
  SecondAngle = 0
FEATURE [Part::Cylinder] Cylinder097
  Angle = 360
  AttacherType = Attacher::AttachEngine3D
  FirstAngle = 0
  Height = 5
  Radius = 10
  SecondAngle = 0
FEATURE [Part::MultiFuse] Fusion028  label="Switch"
  Placement = pos=(83,7.5,14) rot=(0,-1,0;1.5708rad)
  Shapes = -> [Cylinder096,Cylinder097]
FEATURE [Part::Cylinder] Cylinder098  label="Ethernet"
  Angle = 360
  AttacherType = Attacher::AttachEngine3D
  FirstAngle = 0
  Height = 36
  Radius = 10.5
  SecondAngle = 0
FEATURE [Part::Cylinder] Cylinder099  label="Ethernet001"
  Angle = 360
  AttacherType = Attacher::AttachEngine3D
  FirstAngle = 0
  Height = 2.25
  Placement = pos=(0,0,13.5) rot=(0,0,1;0rad)
  Radius = 15
  SecondAngle = 0
FEATURE [Part::MultiFuse] Fusion029  label="EthenetCut"
  Placement = pos=(34,5,124.5) rot=(0,-1,0;1.5708rad)
  Shapes = -> [Cylinder098,Cylinder099]
FEATURE [Part::Box] Box038  label="ethernetHold"
  AttacherType = Attacher::AttachEngine3D
  Height = 34
  Length = 3
  Placement = pos=(15.3,24,109.5) rot=(1,0,0;1.5708rad)
  Width = 37
FEATURE [Part::Cylinder] Cylinder100  label="Ethernet002"
  Angle = 360
  AttacherType = Attacher::AttachEngine3D
  FirstAngle = 0
  Height = 36
  Radius = 10.5
  SecondAngle = 0
FEATURE [Part::Cylinder] Cylinder101  label="Ethernet003"
  Angle = 360
  AttacherType = Attacher::AttachEngine3D
  FirstAngle = 0
  Height = 2.25
  Placement = pos=(0,0,13.5) rot=(0,0,1;0rad)
  Radius = 15
  SecondAngle = 0
FEATURE [Part::MultiFuse] Fusion030  label="Ethenet001"
  Placement = pos=(34,5,124.5) rot=(0,-1,0;1.5708rad)
  Shapes = -> [Cylinder100,Cylinder101]
FEATURE [Part::MultiFuse] Fusion031  label="baseBottom004"
  Shapes = -> [Cut045,Box038]
FEATURE [Part::Cylinder] Cylinder102  label="hookReinforment"
  Angle = 90
  AttacherType = Attacher::AttachEngine3D
  FirstAngle = 0
  Height = 60
  Placement = pos=(9,24,146) rot=(0.57735,-0.57735,0.57735;4.18879rad)
  Radius = 5
  SecondAngle = 0
FEATURE [Part::FeaturePython] Tube  label="hookCut"  # WARN: FeaturePython — macro-defined, semantics opaque (R4)
  AttacherType = Attacher::AttachEngine3D
  Height = 10
  InnerRadius = 5
  OuterRadius = 7
  Placement = pos=(34,24,146) rot=(0,1,0;1.5708rad)
FEATURE [Part::MultiFuse] Fusion032  label="baseBottom005"
  Shapes = -> [Fusion031,Cylinder102]
FEATURE [Part::MultiFuse] Fusion033  label="baseBottomCuts"
  Shapes = -> [Fusion029,Fusion028,Tube]
FEATURE [Part::Cut] Cut046  label="baseBottom006"
  Base = -> Fusion032
  Tool = -> Fusion033
FEATURE [Part::Box] Box042  label="Cube034"
  AttacherType = Attacher::AttachEngine3D
  Height = 12
  Length = 6
  Placement = pos=(3,0,44) rot=(0,0,1;0rad)
  Width = 2
FEATURE [Part::Cylinder] Cylinder105
  Angle = 360
  AttacherType = Attacher::AttachEngine3D
  FirstAngle = 0
  Height = 2
  Placement = pos=(6,0,44) rot=(0,0.707107,0.707107;3.14159rad)
  Radius = 3
  SecondAngle = 0
FEATURE [Part::Cylinder] Cylinder106
  Angle = 360
  AttacherType = Attacher::AttachEngine3D
  FirstAngle = 0
  Height = 2
  Placement = pos=(6,1.2e-14,56) rot=(0,0.707107,0.707107;3.14159rad)
  Radius = 3
  SecondAngle = 0
FEATURE [Part::Box] Box043  label="lightCut"
  AttacherType = Attacher::AttachEngine3D
  Height = 5
  Length = 5
  Placement = pos=(54.5,-16,-6) rot=(0,0,1;0rad)
  Width = 5
FEATURE [Part::Box] Box045  label="Cube036"
  AttacherType = Attacher::AttachEngine3D
  Height = 2
  Length = 20
  Placement = pos=(0,0,0) rot=(0,-1,0;0.785398rad)
  Width = 10
FEATURE [Part::Box] Box046  label="Cube037"
  AttacherType = Attacher::AttachEngine3D
  Height = 2
  Length = 20
  Placement = pos=(0,0,10) rot=(0,-1,0;0.785398rad)
  Width = 10
FEATURE [Part::Box] Box047  label="Cube038"
  AttacherType = Attacher::AttachEngine3D
  Height = 2
  Length = 20
  Placement = pos=(0,0,20) rot=(0,-1,0;0.785398rad)
  Width = 10
FEATURE [Part::Box] Box048  label="Cube039"
  AttacherType = Attacher::AttachEngine3D
  Height = 2
  Length = 20
  Placement = pos=(0,0,30) rot=(0,-1,0;0.785398rad)
  Width = 10
FEATURE [Part::Box] Box049  label="Cube040"
  AttacherType = Attacher::AttachEngine3D
  Height = 2
  Length = 10
  Placement = pos=(0,0,40) rot=(0,-1,0;0.785398rad)
  Width = 10
FEATURE [Part::Box] Box050  label="Cube041"
  AttacherType = Attacher::AttachEngine3D
  Height = 2
  Length = 20
  Placement = pos=(0,0,50) rot=(0,-1,0;0.785398rad)
  Width = 10
FEATURE [Part::Box] Box051  label="Cube042"
  AttacherType = Attacher::AttachEngine3D
  Height = 2
  Length = 20
  Placement = pos=(0,0,60) rot=(0,-1,0;0.785398rad)
  Width = 10
FEATURE [Part::Box] Box052  label="Cube043"
  AttacherType = Attacher::AttachEngine3D
  Height = 2
  Length = 20
  Placement = pos=(0,0,70) rot=(0,-1,0;0.785398rad)
  Width = 10
FEATURE [Part::Box] Box053  label="Cube044"
  AttacherType = Attacher::AttachEngine3D
  Height = 2
  Length = 20
  Placement = pos=(0,0,80) rot=(0,-1,0;0.785398rad)
  Width = 10
FEATURE [Part::Box] Box054  label="Cube045"
  AttacherType = Attacher::AttachEngine3D
  Height = 2
  Length = 20
  Placement = pos=(0,0,90) rot=(0,-1,0;0.785398rad)
  Width = 10
FEATURE [Part::Box] Box055  label="Cube046"
  AttacherType = Attacher::AttachEngine3D
  Height = 2
  Length = 20
  Placement = pos=(0,0,1000) rot=(0,-1,0;0.785398rad)
  Width = 10
FEATURE [Part::MultiFuse] Fusion036
  Placement = pos=(-4,-10,15) rot=(0,0,1;0rad)
  Shapes = -> [Box045,Box046,Box047,Box048,Box049,Box050,Box051,Box052,Box053,Box054,Box055]
FEATURE [Part::Box] Box056  label="Cube047"
  AttacherType = Attacher::AttachEngine3D
  Height = 2
  Length = 20
  Placement = pos=(0,0,0) rot=(0,-1,0;0.785398rad)
  Width = 10
FEATURE [Part::Box] Box057  label="Cube048"
  AttacherType = Attacher::AttachEngine3D
  Height = 2
  Length = 20
  Placement = pos=(0,0,10) rot=(0,-1,0;0.785398rad)
  Width = 10
FEATURE [Part::Box] Box058  label="Cube049"
  AttacherType = Attacher::AttachEngine3D
  Height = 2
  Length = 20
  Placement = pos=(0,0,20) rot=(0,-1,0;0.785398rad)
  Width = 10
FEATURE [Part::Box] Box059  label="Cube050"
  AttacherType = Attacher::AttachEngine3D
  Height = 2
  Length = 20
  Placement = pos=(0,0,30) rot=(0,-1,0;0.785398rad)
  Width = 10
FEATURE [Part::Box] Box060  label="Cube051"
  AttacherType = Attacher::AttachEngine3D
  Height = 2
  Length = 10
  Placement = pos=(0,0,40) rot=(0,-1,0;0.785398rad)
  Width = 10
FEATURE [Part::Box] Box061  label="Cube052"
  AttacherType = Attacher::AttachEngine3D
  Height = 2
  Length = 20
  Placement = pos=(0,0,50) rot=(0,-1,0;0.785398rad)
  Width = 10
FEATURE [Part::Box] Box062  label="Cube053"
  AttacherType = Attacher::AttachEngine3D
  Height = 2
  Length = 20
  Placement = pos=(0,0,60) rot=(0,-1,0;0.785398rad)
  Width = 10
FEATURE [Part::Box] Box063  label="Cube054"
  AttacherType = Attacher::AttachEngine3D
  Height = 2
  Length = 20
  Placement = pos=(0,0,70) rot=(0,-1,0;0.785398rad)
  Width = 10
FEATURE [Part::Box] Box064  label="Cube055"
  AttacherType = Attacher::AttachEngine3D
  Height = 2
  Length = 10
  Placement = pos=(0,0,80) rot=(0,-1,0;0.785398rad)
  Width = 10
FEATURE [Part::Box] Box065  label="Cube056"
  AttacherType = Attacher::AttachEngine3D
  Height = 2
  Length = 20
  Placement = pos=(0,0,90) rot=(0,-1,0;0.785398rad)
  Width = 10
FEATURE [Part::Box] Box066  label="Cube057"
  AttacherType = Attacher::AttachEngine3D
  Height = 2
  Length = 20
  Placement = pos=(0,0,1000) rot=(0,-1,0;0.785398rad)
  Width = 10
FEATURE [Part::MultiFuse] Fusion037
  Placement = pos=(82,0,15) rot=(0,0,1;3.14159rad)
  Shapes = -> [Box056,Box057,Box058,Box059,Box060,Box061,Box062,Box063,Box064,Box065,Box066]
FEATURE [Part::MultiFuse] Fusion038  label="vents"
  Placement = pos=(0,-32,0) rot=(0,0,1;0rad)
  Shapes = -> [Fusion036,Fusion037]
FEATURE [Part::Box] Box070  label="Cube059"
  AttacherType = Attacher::AttachEngine3D
  Height = 2.5
  Length = 58
  Placement = pos=(68,24,21) rot=(0,0,1;3.14159rad)
  Width = 10
FEATURE [Part::Box] Box071  label="Cube060"
  AttacherType = Attacher::AttachEngine3D
  Height = 10.5
  Length = 58
  Placement = pos=(68,24,21) rot=(0,0,1;3.14159rad)
  Width = 10
FEATURE [Part::Cylinder] Cylinder109
  Angle = 360
  AttacherType = Attacher::AttachEngine3D
  FirstAngle = 0
  Height = 78
  Placement = pos=(-6.8e-15,11.4,30.7) rot=(0,1,0;1.5708rad)
  Radius = 12.5
  SecondAngle = 0
FEATURE [Part::Cut] Cut056
  Base = -> Box071
  Tool = -> Cylinder109
FEATURE [Part::Feature] Solid008  label="m4Nut"
  Placement = pos=(5,-19,141) rot=(1,0,0;4.71239rad)
  shape: bbox 8.084 x 2.201 x 8.084 mm, 26 faces (baked)
FEATURE [Part::FeaturePython] Clone  label="m4Nut001"  # Draft clone (typed FeaturePython)
  AttacherType = Attacher::AttachEngine3D
  Fuse = false
  Objects = -> [Solid008]
  Placement = pos=(5,-22.5,141) rot=(1,0,0;4.71239rad)
  Scale = (1,1,4)
FEATURE [Part::Cylinder] Cylinder110  label="m4SupportDisk001"
  Angle = 360
  AttacherType = Attacher::AttachEngine3D
  FirstAngle = 0
  Height = 15
  Placement = pos=(5,-20.09,141) rot=(-1,0,0;1.5708rad)
  Radius = 5.69
  SecondAngle = 0
FEATURE [Part::Feature] Clone001  label="m4Nut002"
  Placement = pos=(5,-22.5,141) rot=(-1,0,0;1.5708rad)
  shape: bbox 8.083 x 8.8 x 9.333 mm, 26 faces (baked)
FEATURE [Part::Cut] Cut057
  Base = -> Clone001
  Placement = pos=(0,0.5,0) rot=(0,0,1;0rad)
  Tool = -> Cylinder110
FEATURE [Part::MultiFuse] Fusion044
  Shapes = -> [Cut057,Solid008]
FEATURE [Part::Cut] Cut058  label="m4Hold"
  Base = -> Cylinder073
  Tool = -> Fusion044
FEATURE [Part::Cylinder] Cylinder111  label="m4HoleBaseCut008"
  Angle = 360
  AttacherType = Attacher::AttachEngine3D
  FirstAngle = 0
  Height = 79
  Placement = pos=(5,26,141) rot=(0,-0.707107,0.707107;3.14159rad)
  Radius = 2.1
  SecondAngle = 0
FEATURE [Part::Cut] Cut059  label="m4Hold001"
  Base = -> Cut058
  Tool = -> Cylinder111
FEATURE [Part::Feature] Clone002  label="m4Nut003"
  Placement = pos=(5,-22.5,141) rot=(-1,0,0;1.5708rad)
  shape: bbox 8.083 x 8.8 x 9.333 mm, 26 faces (baked)
FEATURE [Part::Cylinder] Cylinder112  label="m4SupportDisk002"
  Angle = 360
  AttacherType = Attacher::AttachEngine3D
  FirstAngle = 0
  Height = 15
  Placement = pos=(5,-25,141) rot=(-1,0,0;1.5708rad)
  Radius = 5.69
  SecondAngle = 0
FEATURE [Part::Cylinder] Cylinder113  label="m4SupportDisk003"
  Angle = 360
  AttacherType = Attacher::AttachEngine3D
  FirstAngle = 0
  Height = 15
  Placement = pos=(5,-20.09,141) rot=(-1,0,0;1.5708rad)
  Radius = 5.69
  SecondAngle = 0
FEATURE [Part::Cut] Cut060
  Base = -> Clone002
  Placement = pos=(0,0.5,0) rot=(0,0,1;0rad)
  Tool = -> Cylinder113
FEATURE [Part::Cylinder] Cylinder114  label="m4HoleBaseCut009"
  Angle = 360
  AttacherType = Attacher::AttachEngine3D
  FirstAngle = 0
  Height = 79
  Placement = pos=(5,26,141) rot=(0,0.707107,-0.707107;3.14159rad)
  Radius = 2.1
  SecondAngle = 0
FEATURE [Part::Feature] Solid009  label="m4Nut004"
  Placement = pos=(5,-19,141) rot=(-1,0,0;1.5708rad)
  shape: bbox 8.084 x 2.201 x 8.084 mm, 26 faces (baked)
FEATURE [Part::MultiFuse] Fusion045
  Shapes = -> [Cut060,Solid009]
FEATURE [Part::Cut] Cut061  label="m4Hold002"
  Base = -> Cylinder112
  Tool = -> Fusion045
FEATURE [Part::Cut] Cut062  label="m4Hold003"
  Base = -> Cut061
  Placement = pos=(68,0,0) rot=(0,0,1;0rad)
  Tool = -> Cylinder114
FEATURE [Part::Feature] Clone003  label="m4Nut005"
  Placement = pos=(5,-22.5,141) rot=(-1,0,0;1.5708rad)
  shape: bbox 8.083 x 8.8 x 9.333 mm, 26 faces (baked)
FEATURE [Part::Cylinder] Cylinder115  label="m4SupportDisk004"
  Angle = 360
  AttacherType = Attacher::AttachEngine3D
  FirstAngle = 0
  Height = 15
  Placement = pos=(5,-25,141) rot=(-1,0,0;1.5708rad)
  Radius = 5.69
  SecondAngle = 0
FEATURE [Part::Cylinder] Cylinder116  label="m4SupportDisk005"
  Angle = 360
  AttacherType = Attacher::AttachEngine3D
  FirstAngle = 0
  Height = 15
  Placement = pos=(5,-20.09,141) rot=(-1,0,0;1.5708rad)
  Radius = 5.69
  SecondAngle = 0
FEATURE [Part::Cut] Cut063
  Base = -> Clone003
  Placement = pos=(0,0.5,0) rot=(0,0,1;0rad)
  Tool = -> Cylinder116
FEATURE [Part::Cylinder] Cylinder117  label="m4HoleBaseCut010"
  Angle = 360
  AttacherType = Attacher::AttachEngine3D
  FirstAngle = 0
  Height = 79
  Placement = pos=(5,26,141) rot=(0,0.707107,-0.707107;3.14159rad)
  Radius = 2.1
  SecondAngle = 0
FEATURE [Part::Feature] Solid010  label="m4Nut006"
  Placement = pos=(5,-19,141) rot=(-1,0,0;1.5708rad)
  shape: bbox 8.084 x 2.201 x 8.084 mm, 26 faces (baked)
FEATURE [Part::MultiFuse] Fusion046
  Shapes = -> [Cut063,Solid010]
FEATURE [Part::Cut] Cut064  label="m4Hold004"
  Base = -> Cylinder115
  Tool = -> Fusion046
FEATURE [Part::Cut] Cut065  label="m4Hold005"
  Base = -> Cut064
  Placement = pos=(68,0,-136) rot=(0,0,1;0rad)
  Tool = -> Cylinder117
FEATURE [Part::Feature] Clone004  label="m4Nut007"
  Placement = pos=(5,-22.5,141) rot=(-1,0,0;1.5708rad)
  shape: bbox 8.083 x 8.8 x 9.333 mm, 26 faces (baked)
FEATURE [Part::Cylinder] Cylinder118  label="m4SupportDisk006"
  Angle = 360
  AttacherType = Attacher::AttachEngine3D
  FirstAngle = 0
  Height = 15
  Placement = pos=(5,-25,141) rot=(-1,0,0;1.5708rad)
  Radius = 5.69
  SecondAngle = 0
FEATURE [Part::Cylinder] Cylinder119  label="m4SupportDisk007"
  Angle = 360
  AttacherType = Attacher::AttachEngine3D
  FirstAngle = 0
  Height = 15
  Placement = pos=(5,-20.09,141) rot=(-1,0,0;1.5708rad)
  Radius = 5.69
  SecondAngle = 0
FEATURE [Part::Cut] Cut066
  Base = -> Clone004
  Placement = pos=(0,0.5,0) rot=(0,0,1;0rad)
  Tool = -> Cylinder119
FEATURE [Part::Cylinder] Cylinder120  label="m4HoleBaseCut011"
  Angle = 360
  AttacherType = Attacher::AttachEngine3D
  FirstAngle = 0
  Height = 79
  Placement = pos=(5,26,141) rot=(0,0.707107,-0.707107;3.14159rad)
  Radius = 2.1
  SecondAngle = 0
FEATURE [Part::Feature] Solid011  label="m4Nut008"
  Placement = pos=(5,-19,141) rot=(-1,0,0;1.5708rad)
  shape: bbox 8.084 x 2.201 x 8.084 mm, 26 faces (baked)
FEATURE [Part::MultiFuse] Fusion047
  Shapes = -> [Cut066,Solid011]
FEATURE [Part::Cut] Cut067  label="m4Hold006"
  Base = -> Cylinder118
  Tool = -> Fusion047
FEATURE [Part::Cut] Cut068  label="m4Hold007"
  Base = -> Cut067
  Placement = pos=(0,0,-136) rot=(0,0,1;0rad)
  Tool = -> Cylinder120
FEATURE [Part::MultiFuse] Fusion048  label="m4Holds"
  Shapes = -> [Cut059,Cut062,Cut065,Cut068]
FEATURE [Part::MultiFuse] Fusion049  label="top"
  Shapes = -> [Cut038,Fusion048]
FEATURE [Part::Feature] Solid013  label="m4Nut011"
  Placement = pos=(5,-19,141) rot=(-1,0,0;1.5708rad)
  shape: bbox 8.084 x 2.201 x 8.084 mm, 26 faces (baked)
FEATURE [Part::Feature] Clone006  label="m4Nut012"
  Placement = pos=(5,-22.5,141) rot=(-1,0,0;1.5708rad)
  shape: bbox 8.083 x 8.8 x 9.333 mm, 26 faces (baked)
FEATURE [Part::Cylinder] Cylinder122  label="m4SupportDisk009"
  Angle = 360
  AttacherType = Attacher::AttachEngine3D
  FirstAngle = 0
  Height = 15
  Placement = pos=(5,-20.09,141) rot=(-1,0,0;1.5708rad)
  Radius = 5.69
  SecondAngle = 0
FEATURE [Part::Cut] Cut070
  Base = -> Clone006
  Placement = pos=(0,0.5,0) rot=(0,0,1;0rad)
  Tool = -> Cylinder122
FEATURE [Part::MultiFuse] Fusion051
  Shapes = -> [Cut070,Solid013]
FEATURE [Part::Feature] Clone007  label="m4Nut013"
  Placement = pos=(5,-22.5,141) rot=(-1,0,0;1.5708rad)
  shape: bbox 8.083 x 8.8 x 9.333 mm, 26 faces (baked)
FEATURE [Part::Cylinder] Cylinder123  label="m4SupportDisk010"
  Angle = 360
  AttacherType = Attacher::AttachEngine3D
  FirstAngle = 0
  Height = 15
  Placement = pos=(5,-20.09,141) rot=(-1,0,0;1.5708rad)
  Radius = 5.69
  SecondAngle = 0
FEATURE [Part::Cut] Cut071
  Base = -> Clone007
  Placement = pos=(0,0.5,0) rot=(0,0,1;0rad)
  Tool = -> Cylinder123
FEATURE [Part::Feature] Solid014  label="m4Nut014"
  Placement = pos=(5,-19,141) rot=(-1,0,0;1.5708rad)
  shape: bbox 8.084 x 2.201 x 8.084 mm, 26 faces (baked)
FEATURE [Part::MultiFuse] Fusion052
  Placement = pos=(68,0,0) rot=(0,0,1;0rad)
  Shapes = -> [Cut071,Solid014]
FEATURE [Part::MultiFuse] Fusion053
  Shapes = -> [Fusion051,Fusion052]
FEATURE [Part::Feature] Clone008  label="m4Nut015"
  Placement = pos=(5,-22.5,141) rot=(-1,0,0;1.5708rad)
  shape: bbox 8.083 x 8.8 x 9.333 mm, 26 faces (baked)
FEATURE [Part::Feature] Clone009  label="m4Nut016"
  Placement = pos=(5,-22.5,141) rot=(-1,0,0;1.5708rad)
  shape: bbox 8.083 x 8.8 x 9.333 mm, 26 faces (baked)
FEATURE [Part::Cylinder] Cylinder124  label="m4SupportDisk011"
  Angle = 360
  AttacherType = Attacher::AttachEngine3D
  FirstAngle = 0
  Height = 15
  Placement = pos=(5,-20.09,141) rot=(-1,0,0;1.5708rad)
  Radius = 5.69
  SecondAngle = 0
FEATURE [Part::Cut] Cut072
  Base = -> Clone008
  Placement = pos=(0,0.5,0) rot=(0,0,1;0rad)
  Tool = -> Cylinder124
FEATURE [Part::Cylinder] Cylinder125  label="m4SupportDisk012"
  Angle = 360
  AttacherType = Attacher::AttachEngine3D
  FirstAngle = 0
  Height = 15
  Placement = pos=(5,-20.09,141) rot=(-1,0,0;1.5708rad)
  Radius = 5.69
  SecondAngle = 0
FEATURE [Part::Cut] Cut073
  Base = -> Clone009
  Placement = pos=(0,0.5,0) rot=(0,0,1;0rad)
  Tool = -> Cylinder125
FEATURE [Part::Feature] Solid015  label="m4Nut017"
  Placement = pos=(5,-19,141) rot=(-1,0,0;1.5708rad)
  shape: bbox 8.084 x 2.201 x 8.084 mm, 26 faces (baked)
FEATURE [Part::MultiFuse] Fusion054
  Shapes = -> [Cut072,Solid015]
FEATURE [Part::Feature] Solid016  label="m4Nut018"
  Placement = pos=(5,-19,141) rot=(-1,0,0;1.5708rad)
  shape: bbox 8.084 x 2.201 x 8.084 mm, 26 faces (baked)
FEATURE [Part::MultiFuse] Fusion055
  Placement = pos=(68,0,0) rot=(0,0,1;0rad)
  Shapes = -> [Cut073,Solid016]
FEATURE [Part::MultiFuse] Fusion056
  Placement = pos=(0,0,-136) rot=(0,0,1;0rad)
  Shapes = -> [Fusion054,Fusion055]
FEATURE [Part::MultiFuse] Fusion057
  Placement = pos=(0,-3,0) rot=(0,0,1;0rad)
  Shapes = -> [Fusion056,Fusion053]
FEATURE [Part::Cut] Cut074  label="top001"
  Base = -> Fusion049
  Tool = -> Fusion057
FEATURE [Part::MultiFuse] Fusion058  label="topCuts"
  Shapes = -> [Fusion038,Box043]
FEATURE [Part::Cut] Cut075
  Base = -> Cut074
  Tool = -> Fusion058
FEATURE [Part::MultiFuse] Fusion059  label="top002"
  Shapes = -> [Cut075,Cut043]
FEATURE [Part::Box] Box072  label="Cube061"
  AttacherType = Attacher::AttachEngine3D
  Height = 1.5
  Length = 36
  Width = 29
FEATURE [Part::Box] Box073  label="Cube062"
  AttacherType = Attacher::AttachEngine3D
  Height = 5.5
  Length = 36
  Placement = pos=(0,0,3.6) rot=(0,0,1;0rad)
  Width = 29
FEATURE [Part::Feature] logo3mmWidth001_solid  label="logo3mmWidth001 (Solid)"
  shape: bbox 30 x 22.21 x 4.944 mm, 7244 faces (baked)
FEATURE [Part::MultiFuse] Fusion060
  Shapes = -> [Box072,logo3mmWidth001_solid]
FEATURE [Part::Cut] Cut076  label="logo004"
  Base = -> Fusion060
  Placement = pos=(21,-42.5,14.6) rot=(1,0,0;1.5708rad)
  Tool = -> Box073
FEATURE [Part::Cut] Cut077  label="top003"
  Base = -> Fusion059
  Tool = -> Cut076
FEATURE [Part::MultiFuse] Fusion035  label="voltaicCut"
  Placement = pos=(33,24,31.5) rot=(0,0,1;0rad)
  Shapes = -> [Cylinder106,Cylinder105,Box042]
FEATURE [Part::MultiFuse] Fusion042  label="baseBottom007"
  Shapes = -> [Cut056,Box070]
FEATURE [Part::Box] Box074  label="usbCut002"
  AttacherType = Attacher::AttachEngine3D
  Height = 10
  Length = 82
  Width = 20
FEATURE [Part::Box] Box075  label="Cube063"
  AttacherType = Attacher::AttachEngine3D
  Height = 10
  Length = 82
  Width = 5
FEATURE [Part::Box] Box076  label="Cube064"
  AttacherType = Attacher::AttachEngine3D
  Height = 10
  Length = 82
  Width = 5
FEATURE [Part::Cylinder] Cylinder126
  Angle = 180
  AttacherType = Attacher::AttachEngine3D
  FirstAngle = 0
  Height = 82
  Placement = pos=(0,5,5) rot=(0.707107,0,0.707107;3.14159rad)
  Radius = 5
  SecondAngle = 0
FEATURE [Part::Cut] Cut078  label="cornerCuts002"
  Base = -> Box075
  Tool = -> Cylinder126
FEATURE [Part::Cylinder] Cylinder127
  Angle = 180
  AttacherType = Attacher::AttachEngine3D
  FirstAngle = 0
  Height = 82
  Placement = pos=(0,5,5) rot=(0.707107,0,0.707107;3.14159rad)
  Radius = 5
  SecondAngle = 0
FEATURE [Part::Cut] Cut079  label="cornerCuts003"
  Base = -> Box076
  Placement = pos=(0,20,10) rot=(1,0,0;3.14159rad)
  Tool = -> Cylinder127
FEATURE [Part::MultiFuse] Fusion061
  Shapes = -> [Cut078,Cut079]
FEATURE [Part::Cut] Cut080  label="usbCut003"
  Base = -> Box074
  Placement = pos=(-50,16,68) rot=(1,0,0;1.5708rad)
  Tool = -> Fusion061
FEATURE [Part::Box] Box077  label="usbCut004"
  AttacherType = Attacher::AttachEngine3D
  Height = 10
  Length = 82
  Width = 20
FEATURE [Part::Box] Box078  label="Cube065"
  AttacherType = Attacher::AttachEngine3D
  Height = 10
  Length = 82
  Width = 5
FEATURE [Part::Box] Box079  label="Cube066"
  AttacherType = Attacher::AttachEngine3D
  Height = 10
  Length = 82
  Width = 5
FEATURE [Part::Cylinder] Cylinder128
  Angle = 180
  AttacherType = Attacher::AttachEngine3D
  FirstAngle = 0
  Height = 82
  Placement = pos=(0,5,5) rot=(0.707107,0,0.707107;3.14159rad)
  Radius = 5
  SecondAngle = 0
FEATURE [Part::Cut] Cut082  label="cornerCuts004"
  Base = -> Box078
  Tool = -> Cylinder128
FEATURE [Part::Cylinder] Cylinder129
  Angle = 180
  AttacherType = Attacher::AttachEngine3D
  FirstAngle = 0
  Height = 82
  Placement = pos=(0,5,5) rot=(0.707107,0,0.707107;3.14159rad)
  Radius = 5
  SecondAngle = 0
FEATURE [Part::Cut] Cut083  label="cornerCuts005"
  Base = -> Box079
  Placement = pos=(0,20,10) rot=(1,0,0;3.14159rad)
  Tool = -> Cylinder129
FEATURE [Part::MultiFuse] Fusion062
  Shapes = -> [Cut082,Cut083]
FEATURE [Part::Cut] Cut084  label="usbCut005"
  Base = -> Box077
  Placement = pos=(50,17,68) rot=(1,0,0;1.5708rad)
  Tool = -> Fusion062
FEATURE [Part::MultiFuse] Fusion063  label="bottomCuts"
  Shapes = -> [Cut080,Cut084,Fusion035]
FEATURE [Part::Feature] Part__Feature  label="m3Nut"
  Placement = pos=(2.5,8,100.5) rot=(1,0,0;1.5708rad)
  shape: bbox 6.352 x 1.801 x 6.352 mm, 26 faces (baked)
FEATURE [Part::Feature] Part__Feature001  label="m3Nut001"
  Placement = pos=(2.5,7,100.5) rot=(1,0,0;1.5708rad)
  shape: bbox 6.352 x 1.801 x 6.352 mm, 26 faces (baked)
FEATURE [Part::Feature] Part__Feature002  label="m3Nut002"
  Placement = pos=(2.5,6,100.5) rot=(1,0,0;1.5708rad)
  shape: bbox 6.352 x 1.801 x 6.352 mm, 26 faces (baked)
FEATURE [Part::MultiFuse] Fusion064  label="m3Cuts"
  Shapes = -> [Part__Feature002,Part__Feature,Part__Feature001]
FEATURE [Part::Feature] Part__Feature003  label="m3Nut003"
  Placement = pos=(2.5,8,100.5) rot=(1,0,0;1.5708rad)
  shape: bbox 6.352 x 1.801 x 6.352 mm, 26 faces (baked)
FEATURE [Part::Feature] Part__Feature004  label="m3Nut004"
  Placement = pos=(2.5,7,100.5) rot=(1,0,0;1.5708rad)
  shape: bbox 6.352 x 1.801 x 6.352 mm, 26 faces (baked)
FEATURE [Part::Feature] Part__Feature005  label="m3Nut005"
  Placement = pos=(2.5,6,100.5) rot=(1,0,0;1.5708rad)
  shape: bbox 6.352 x 1.801 x 6.352 mm, 26 faces (baked)
FEATURE [Part::MultiFuse] Fusion065  label="m3Cuts001"
  Placement = pos=(73,0,0) rot=(0,0,1;0rad)
  Shapes = -> [Part__Feature005,Part__Feature003,Part__Feature004]
FEATURE [Part::MultiFuse] Fusion066
  Shapes = -> [Fusion065,Fusion064]
FEATURE [Part::Feature] Part__Feature006  label="m3Nut006"
  Placement = pos=(2.5,8,100.5) rot=(1,0,0;1.5708rad)
  shape: bbox 6.352 x 1.801 x 6.352 mm, 26 faces (baked)
FEATURE [Part::Feature] Part__Feature007  label="m3Nut007"
  Placement = pos=(2.5,7,100.5) rot=(1,0,0;1.5708rad)
  shape: bbox 6.352 x 1.801 x 6.352 mm, 26 faces (baked)
FEATURE [Part::Feature] Part__Feature008  label="m3Nut008"
  Placement = pos=(2.5,6,100.5) rot=(1,0,0;1.5708rad)
  shape: bbox 6.352 x 1.801 x 6.352 mm, 26 faces (baked)
FEATURE [Part::MultiFuse] Fusion067  label="m3Cuts002"
  Shapes = -> [Part__Feature008,Part__Feature006,Part__Feature007]
FEATURE [Part::Feature] Part__Feature009  label="m3Nut009"
  Placement = pos=(2.5,8,100.5) rot=(1,0,0;1.5708rad)
  shape: bbox 6.352 x 1.801 x 6.352 mm, 26 faces (baked)
FEATURE [Part::Feature] Part__Feature010  label="m3Nut010"
  Placement = pos=(2.5,7,100.5) rot=(1,0,0;1.5708rad)
  shape: bbox 6.352 x 1.801 x 6.352 mm, 26 faces (baked)
FEATURE [Part::Feature] Part__Feature011  label="m3Nut011"
  Placement = pos=(2.5,6,100.5) rot=(1,0,0;1.5708rad)
  shape: bbox 6.352 x 1.801 x 6.352 mm, 26 faces (baked)
FEATURE [Part::MultiFuse] Fusion068  label="m3Cuts003"
  Placement = pos=(73,0,0) rot=(0,0,1;0rad)
  Shapes = -> [Part__Feature011,Part__Feature009,Part__Feature010]
FEATURE [Part::MultiFuse] Fusion069
  Placement = pos=(0,2,0) rot=(0,0,1;0rad)
  Shapes = -> [Fusion068,Fusion067]
FEATURE [Part::MultiFuse] Fusion070  label="m3Cuts004"
  Shapes = -> [Fusion066,Fusion069]
FEATURE [Part::Feature] Part__Feature012  label="m3Nut012"
  Placement = pos=(2.5,8,100.5) rot=(1,0,0;1.5708rad)
  shape: bbox 6.352 x 1.801 x 6.352 mm, 26 faces (baked)
FEATURE [Part::Feature] Part__Feature013  label="m3Nut013"
  Placement = pos=(2.5,7,100.5) rot=(1,0,0;1.5708rad)
  shape: bbox 6.352 x 1.801 x 6.352 mm, 26 faces (baked)
FEATURE [Part::Feature] Part__Feature014  label="m3Nut014"
  Placement = pos=(2.5,6,100.5) rot=(1,0,0;1.5708rad)
  shape: bbox 6.352 x 1.801 x 6.352 mm, 26 faces (baked)
FEATURE [Part::Feature] Part__Feature018  label="m3Nut018"
  Placement = pos=(2.5,8,100.5) rot=(1,0,0;1.5708rad)
  shape: bbox 6.352 x 1.801 x 6.352 mm, 26 faces (baked)
FEATURE [Part::Feature] Part__Feature019  label="m3Nut019"
  Placement = pos=(2.5,7,100.5) rot=(1,0,0;1.5708rad)
  shape: bbox 6.352 x 1.801 x 6.352 mm, 26 faces (baked)
FEATURE [Part::Feature] Part__Feature020  label="m3Nut020"
  Placement = pos=(2.5,6,100.5) rot=(1,0,0;1.5708rad)
  shape: bbox 6.352 x 1.801 x 6.352 mm, 26 faces (baked)
FEATURE [Part::MultiFuse] Fusion074  label="m3Cuts007"
  Placement = pos=(0,-3,0) rot=(0,0,1;0rad)
  Shapes = -> [Part__Feature020,Part__Feature018,Part__Feature019]
FEATURE [Part::MultiFuse] Fusion071  label="m3Cuts005"
  Shapes = -> [Part__Feature014,Part__Feature012,Part__Feature013]
FEATURE [Part::MultiFuse] Fusion075  label="m3Cuts008"
  Placement = pos=(11,-7,-97) rot=(0,0,1;0rad)
  Shapes = -> [Fusion071,Fusion074]
FEATURE [Part::Feature] Part__Feature021  label="m3Nut021"
  Placement = pos=(2.5,8,100.5) rot=(1,0,0;1.5708rad)
  shape: bbox 6.352 x 1.801 x 6.352 mm, 26 faces (baked)
FEATURE [Part::Feature] Part__Feature022  label="m3Nut022"
  Placement = pos=(2.5,7,100.5) rot=(1,0,0;1.5708rad)
  shape: bbox 6.352 x 1.801 x 6.352 mm, 26 faces (baked)
FEATURE [Part::Feature] Part__Feature023  label="m3Nut023"
  Placement = pos=(2.5,6,100.5) rot=(1,0,0;1.5708rad)
  shape: bbox 6.352 x 1.801 x 6.352 mm, 26 faces (baked)
FEATURE [Part::MultiFuse] Fusion076  label="m3Cuts009"
  Shapes = -> [Part__Feature023,Part__Feature021,Part__Feature022]
FEATURE [Part::Feature] Part__Feature024  label="m3Nut024"
  Placement = pos=(2.5,8,100.5) rot=(1,0,0;1.5708rad)
  shape: bbox 6.352 x 1.801 x 6.352 mm, 26 faces (baked)
FEATURE [Part::Feature] Part__Feature025  label="m3Nut025"
  Placement = pos=(2.5,7,100.5) rot=(1,0,0;1.5708rad)
  shape: bbox 6.352 x 1.801 x 6.352 mm, 26 faces (baked)
FEATURE [Part::Feature] Part__Feature026  label="m3Nut026"
  Placement = pos=(2.5,6,100.5) rot=(1,0,0;1.5708rad)
  shape: bbox 6.352 x 1.801 x 6.352 mm, 26 faces (baked)
FEATURE [Part::MultiFuse] Fusion077  label="m3Cuts010"
  Placement = pos=(0,-3,0) rot=(0,0,1;0rad)
  Shapes = -> [Part__Feature026,Part__Feature024,Part__Feature025]
FEATURE [Part::MultiFuse] Fusion078  label="m3Cuts011"
  Placement = pos=(60,-7,-97) rot=(0,0,1;0rad)
  Shapes = -> [Fusion076,Fusion077]
FEATURE [Part::MultiFuse] Fusion079
  Shapes = -> [Fusion075,Fusion078]
FEATURE [Part::MultiFuse] Fusion080  label="bottomCuts001"
  Shapes = -> [Fusion063,Fusion079]
FEATURE [Part::MultiFuse] Fusion081  label="bottomCuts002"
  Shapes = -> [Fusion070,Fusion080]
FEATURE [Part::MultiFuse] Fusion082  label="bottom"
  Shapes = -> [Cut046,Fusion042]
FEATURE [Part::Cylinder] Cylinder130
  Angle = 360
  AttacherType = Attacher::AttachEngine3D
  FirstAngle = 0
  Height = 20
  Radius = 6
  SecondAngle = 0
FEATURE [Part::Cylinder] Cylinder131
  Angle = 360
  AttacherType = Attacher::AttachEngine3D
  FirstAngle = 0
  Height = 5
  Radius = 7
  SecondAngle = 0
FEATURE [Part::MultiFuse] Fusion083  label="Switch001"
  Placement = pos=(82,7.5,14) rot=(0,-1,0;1.5708rad)
  Shapes = -> [Cylinder130,Cylinder131]
FEATURE [Part::MultiFuse] Fusion084  label="bottomCuts003"
  Shapes = -> [Fusion083,Fusion081]
FEATURE [Part::Box] Box080  label="ethernetHold001"
  AttacherType = Attacher::AttachEngine3D
  Height = 34
  Length = 3
  Placement = pos=(15.3,5,87.5) rot=(1,0,0;1.5708rad)
  Width = 37
FEATURE [Part::Cut] Cut085
  Base = -> Fusion082
  Tool = -> Fusion084
FEATURE [Part::Cut] Cut086  label="bottom001"
  Base = -> Cut085
  Tool = -> Box080
FEATURE [Part::Feature] Part__Feature027  label="m3Nut027"
  Placement = pos=(2.5,8,100.5) rot=(1,0,0;1.5708rad)
  shape: bbox 6.352 x 1.801 x 6.352 mm, 26 faces (baked)
FEATURE [Part::Feature] Part__Feature028  label="m3Nut028"
  Placement = pos=(2.5,7,100.5) rot=(1,0,0;1.5708rad)
  shape: bbox 6.352 x 1.801 x 6.352 mm, 26 faces (baked)
FEATURE [Part::Feature] Part__Feature029  label="m3Nut029"
  Placement = pos=(2.5,6,100.5) rot=(1,0,0;1.5708rad)
  shape: bbox 6.352 x 1.801 x 6.352 mm, 26 faces (baked)
FEATURE [Part::MultiFuse] Fusion085  label="m3Cuts012"
  Placement = pos=(60,-8,-39) rot=(0,0,1;0rad)
  Shapes = -> [Part__Feature029,Part__Feature027,Part__Feature028]
FEATURE [Part::Feature] Part__Feature030  label="m3Nut030"
  Placement = pos=(2.5,8,100.5) rot=(1,0,0;1.5708rad)
  shape: bbox 6.352 x 1.801 x 6.352 mm, 26 faces (baked)
FEATURE [Part::Feature] Part__Feature031  label="m3Nut031"
  Placement = pos=(2.5,7,100.5) rot=(1,0,0;1.5708rad)
  shape: bbox 6.352 x 1.801 x 6.352 mm, 26 faces (baked)
FEATURE [Part::Feature] Part__Feature032  label="m3Nut032"
  Placement = pos=(2.5,6,100.5) rot=(1,0,0;1.5708rad)
  shape: bbox 6.352 x 1.801 x 6.352 mm, 26 faces (baked)
FEATURE [Part::MultiFuse] Fusion086  label="m3Cuts013"
  Placement = pos=(11,-8,-39) rot=(0,0,1;0rad)
  Shapes = -> [Part__Feature032,Part__Feature030,Part__Feature031]
FEATURE [Part::MultiFuse] Fusion087
  Placement = pos=(0,-2,0) rot=(0,0,1;0rad)
  Shapes = -> [Fusion085,Fusion086]
FEATURE [Part::Cut] Cut087  label="c4Hold002"
  Base = -> Cut024
  Tool = -> Fusion087
FEATURE [Part::Cylinder] Cylinder132
  Angle = 360
  AttacherType = Attacher::AttachEngine3D
  FirstAngle = 0
  Height = 8
  Placement = pos=(13.5,-2,3.5) rot=(1,0,0;1.5708rad)
  Radius = 1.6
  SecondAngle = 0
FEATURE [Part::Cylinder] Cylinder133
  Angle = 360
  AttacherType = Attacher::AttachEngine3D
  FirstAngle = 0
  Height = 8
  Placement = pos=(62.5,-2,3.5) rot=(1,0,0;1.5708rad)
  Radius = 1.6
  SecondAngle = 0
FEATURE [Part::Cylinder] Cylinder134
  Angle = 360
  AttacherType = Attacher::AttachEngine3D
  FirstAngle = 0
  Height = 20
  Radius = 6
  SecondAngle = 0
FEATURE [Part::Cylinder] Cylinder135
  Angle = 360
  AttacherType = Attacher::AttachEngine3D
  FirstAngle = 0
  Height = 5
  Radius = 7
  SecondAngle = 0
FEATURE [Part::MultiFuse] Fusion088  label="powerSwitch002"
  Placement = pos=(71,7.5,14) rot=(0,-1,0;1.5708rad)
  Shapes = -> [Cylinder134,Cylinder135]
FEATURE [Part::MultiFuse] Fusion089  label="baseCuts002"
  Shapes = -> [Cylinder133,Cylinder132,Fusion088]
FEATURE [Part::Cut] Cut088  label="bottom002"
  Base = -> Cut086
  Tool = -> Fusion089
